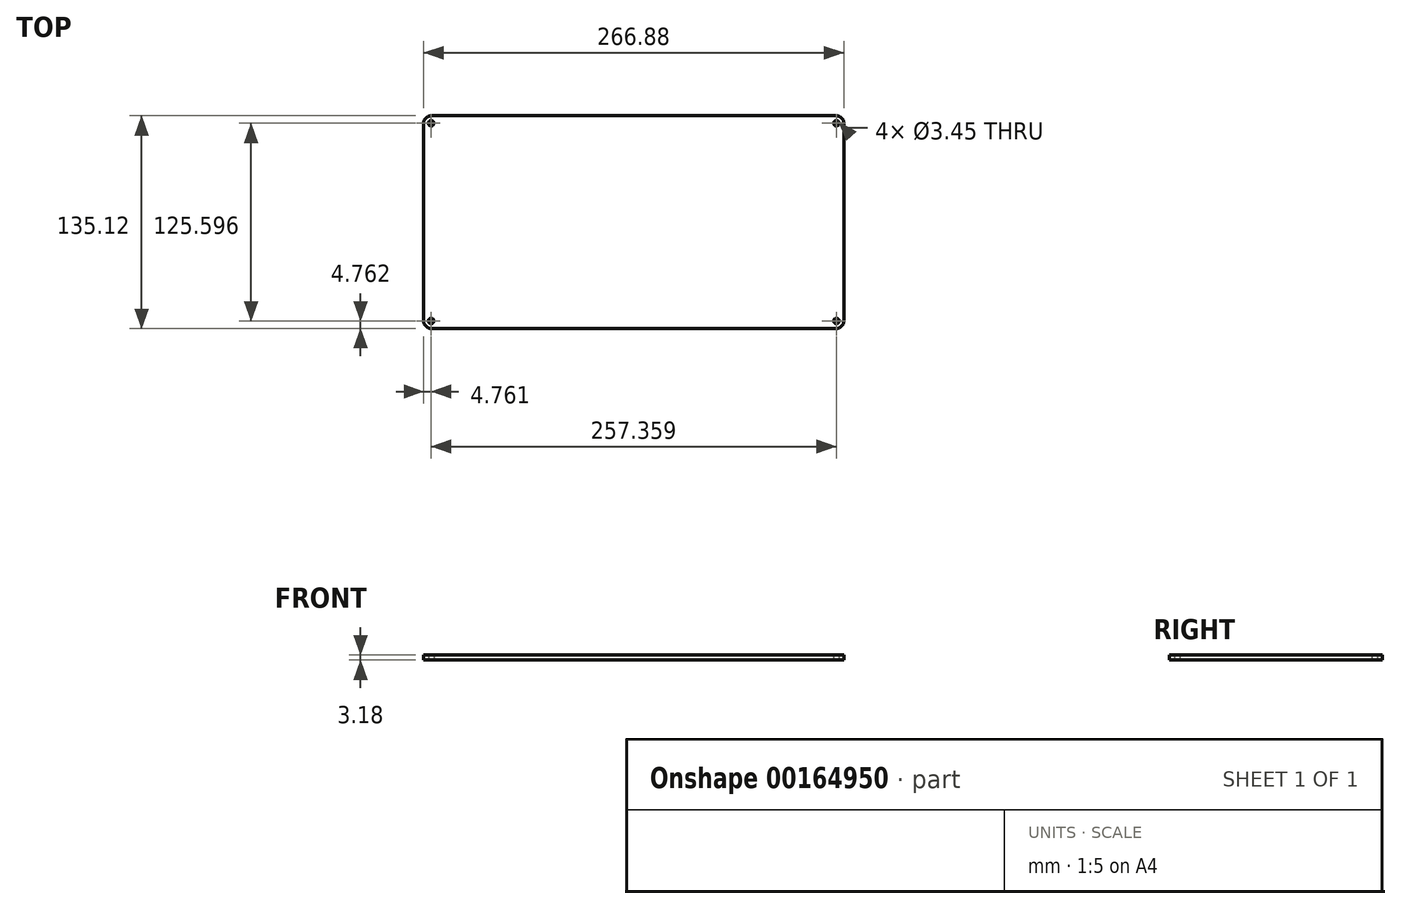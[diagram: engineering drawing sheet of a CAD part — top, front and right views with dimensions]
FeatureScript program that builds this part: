
annotation { "Feature Type Name" : "Feature", "Feature Type Description" : "" }
export const myFeature = defineFeature(function(context is Context, id is Id, definition is map)
    precondition{}
    {
        {
            var Q0;
            Q0=qCreatedBy(makeId("Top.planeOp"),FACE);
            var sketch = newSketch(context, id + "F0", { "sketchPlane" : qUnion([Q0])});
            skLineSegment(sketch, "E0.bottom", {"start": v(-128.68, 62.8) * mm, "end": v(128.68, 62.8) * mm, "construction": true});
            skLineSegment(sketch, "E0.top", {"start": v(-128.68, -62.8) * mm, "end": v(128.68, -62.8) * mm, "construction": true});
            skLineSegment(sketch, "E0.left", {"start": v(-128.68, 62.8) * mm, "end": v(-128.68, -62.8) * mm, "construction": true});
            skLineSegment(sketch, "E0.right", {"start": v(128.68, 62.8) * mm, "end": v(128.68, -62.8) * mm, "construction": true});
            skPoint(sketch, "E0.middle", {"position": v(0, 0) * mm});
            skLineSegment(sketch, "E1", {"start": v(-128.68, 0) * mm, "end": v(-133.44, 0) * mm, "construction": true});
            skLineSegment(sketch, "E2", {"start": v(0, 62.8) * mm, "end": v(0, 67.56) * mm, "construction": true});
            skLineSegment(sketch, "E3.bottom", {"start": v(-133.44, 67.56) * mm, "end": v(133.44, 67.56) * mm});
            skLineSegment(sketch, "E3.top", {"start": v(-133.44, -67.56) * mm, "end": v(133.44, -67.56) * mm});
            skLineSegment(sketch, "E3.left", {"start": v(-133.44, 67.56) * mm, "end": v(-133.44, -67.56) * mm});
            skLineSegment(sketch, "E3.right", {"start": v(133.44, 67.56) * mm, "end": v(133.44, -67.56) * mm});
            skCircle(sketch, "E4", {"center": v(-128.68, -62.8) * mm, "radius": 1.73 * mm});
            skCircle(sketch, "E5", {"center": v(-128.68, 62.8) * mm, "radius": 1.73 * mm});
            skCircle(sketch, "E6", {"center": v(128.68, 62.8) * mm, "radius": 1.73 * mm});
            skCircle(sketch, "E7", {"center": v(128.68, -62.8) * mm, "radius": 1.73 * mm});
            skSolve(sketch);
        }
        {
            var Q0;
            Q0=qSketchRegion(id+"F0",true);
            extrude(context, id + "F1", {"entities" : qUnion([Q0]), "depth" : 3.17 * mm});
        }
        {
            var Q0;
            Q0=makeQuery(id+"F1.opExtrude","SWEPT_EDGE",EDGE,{"disambiguationData":[OSD([sQuery(id+"F0.wireOp",EDGE,"E3.top"),sQuery(id+"F0.wireOp",EDGE,"E3.right")])]});
            var Q1;
            Q1=makeQuery(id+"F1.opExtrude","SWEPT_EDGE",EDGE,{"disambiguationData":[OSD([sQuery(id+"F0.wireOp",EDGE,"E3.bottom"),sQuery(id+"F0.wireOp",EDGE,"E3.right")])]});
            var Q2;
            Q2=makeQuery(id+"F1.opExtrude","SWEPT_EDGE",EDGE,{"disambiguationData":[OSD([sQuery(id+"F0.wireOp",EDGE,"E3.top"),sQuery(id+"F0.wireOp",EDGE,"E3.left")])]});
            var Q3;
            Q3=makeQuery(id+"F1.opExtrude","SWEPT_EDGE",EDGE,{"disambiguationData":[OSD([sQuery(id+"F0.wireOp",EDGE,"E3.bottom"),sQuery(id+"F0.wireOp",EDGE,"E3.left")])]});
            fillet(context, id + "F2", {"entities" : qUnion([Q0, Q1, Q2, Q3]), "radius" : 4.76 * mm, "tangentPropagation" : true, "allowEdgeOverflow" : false});
        }
    });
